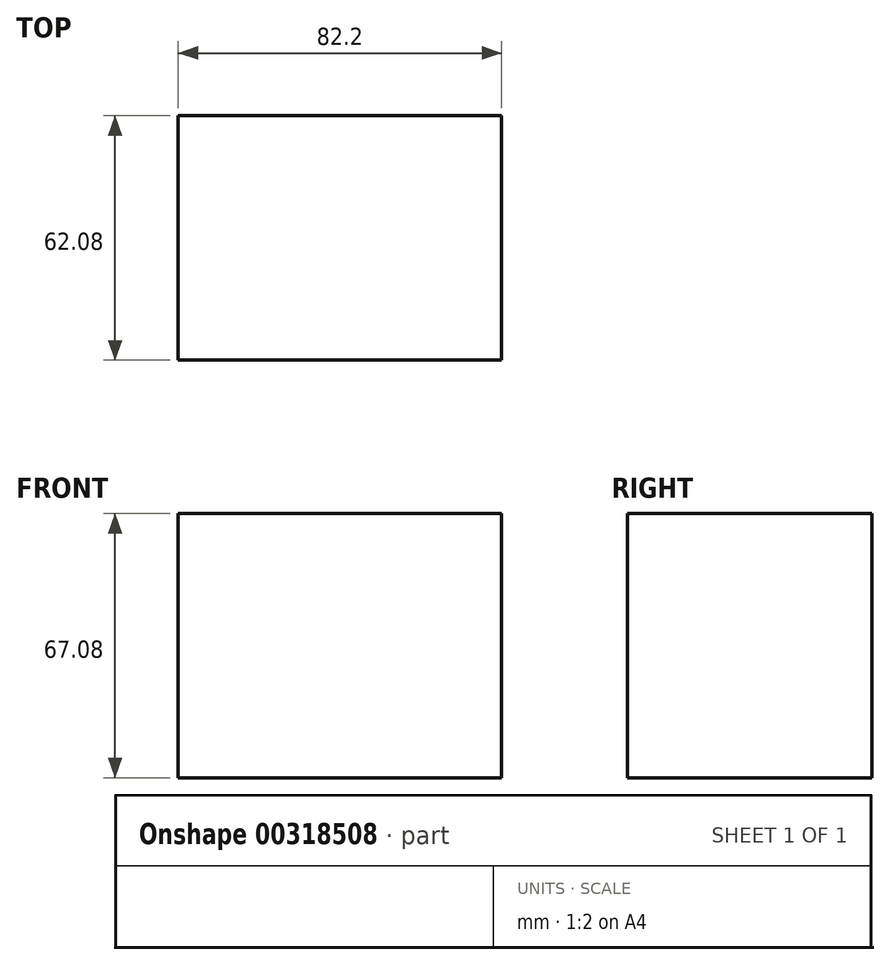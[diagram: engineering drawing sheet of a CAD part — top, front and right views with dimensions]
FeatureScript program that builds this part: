
annotation { "Feature Type Name" : "Feature", "Feature Type Description" : "" }
export const myFeature = defineFeature(function(context is Context, id is Id, definition is map)
    precondition{}
    {
        {
            var Q0;
            Q0=qCreatedBy(makeId("Front.planeOp"),FACE);
            var sketch = newSketch(context, id + "F0", { "sketchPlane" : qUnion([Q0])});
            skLineSegment(sketch, "E0.bottom", {"start": v(-41.1, 33.54) * mm, "end": v(41.1, 33.54) * mm});
            skLineSegment(sketch, "E0.top", {"start": v(-41.1, -33.54) * mm, "end": v(41.1, -33.54) * mm});
            skLineSegment(sketch, "E0.left", {"start": v(-41.1, 33.54) * mm, "end": v(-41.1, -33.54) * mm});
            skLineSegment(sketch, "E0.right", {"start": v(41.1, 33.54) * mm, "end": v(41.1, -33.54) * mm});
            skPoint(sketch, "E0.middle", {"position": v(0, 0) * mm});
            skSolve(sketch);
        }
        {
            var Q0;
            Q0=makeQuery(id+"F0.imprint","IMPRINT",FACE,{"disambiguationData":[TD([[makeQuery(id+"F0.imprint","IMPRINT",EDGE,{"derivedFrom":sQuery(id+"F0.wireOp",EDGE,"E0.bottom")}),-1.0]])]});
            extrude(context, id + "F1", {"entities" : qUnion([Q0]), "depth" : 62.08 * mm});
        }
    });
